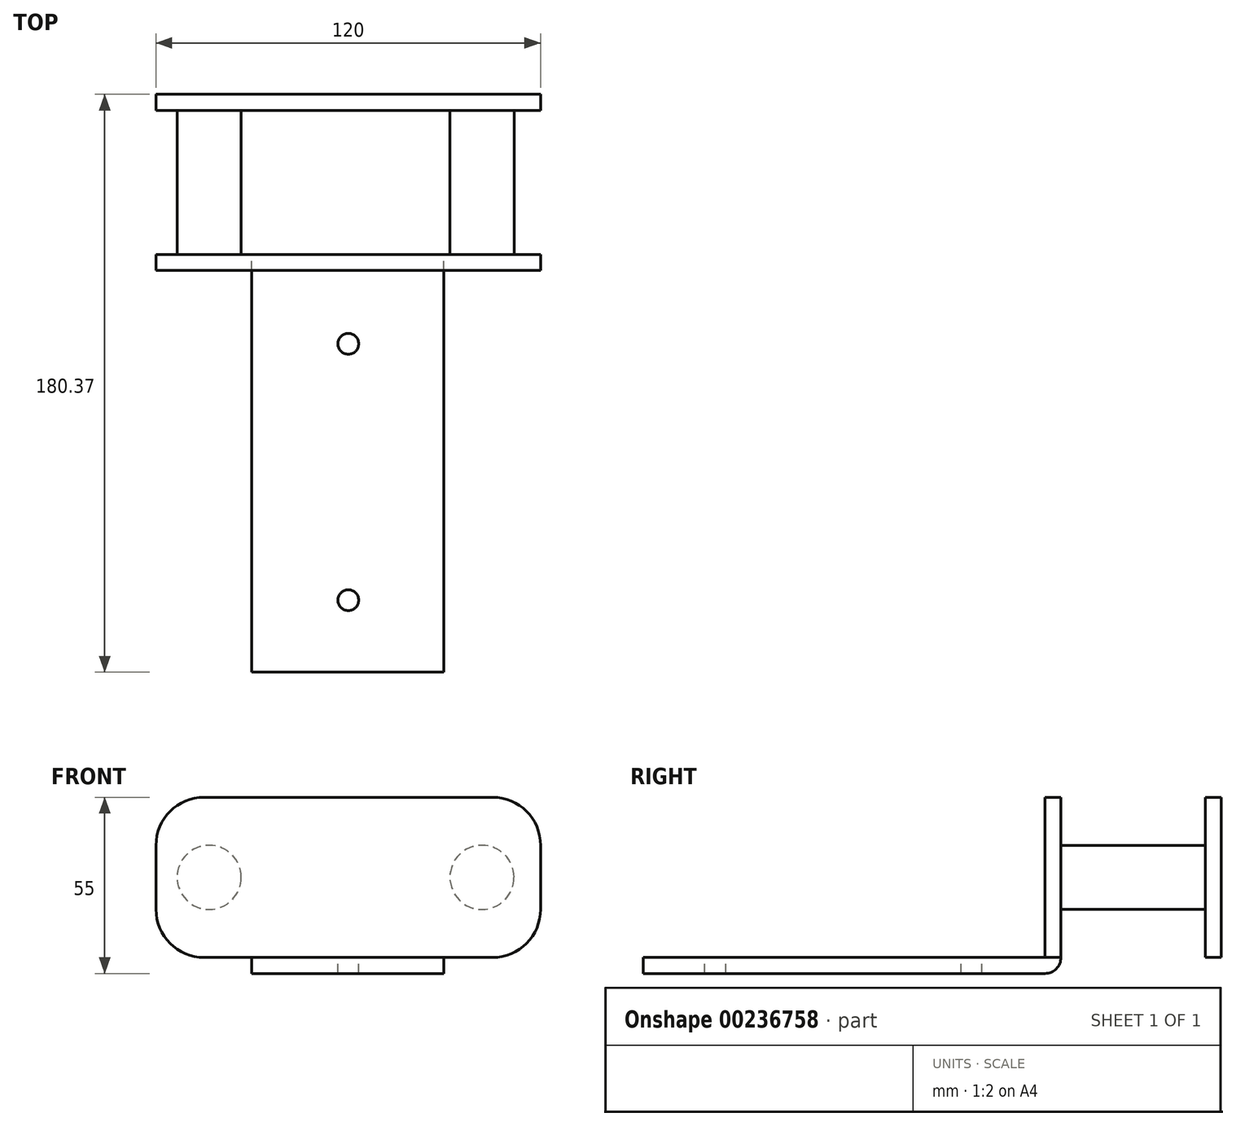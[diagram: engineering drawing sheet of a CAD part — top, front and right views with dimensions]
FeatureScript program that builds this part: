
annotation { "Feature Type Name" : "Feature", "Feature Type Description" : "" }
export const myFeature = defineFeature(function(context is Context, id is Id, definition is map)
    precondition{}
    {
        {
            var Q0;
            Q0=qCreatedBy(makeId("Top.planeOp"),FACE);
            var sketch = newSketch(context, id + "F0", { "sketchPlane" : qUnion([Q0])});
            skLineSegment(sketch, "E0.bottom", {"start": v(29.8, -114.86) * mm, "end": v(-30.2, -114.86) * mm});
            skLineSegment(sketch, "E0.top", {"start": v(29.8, 15.5) * mm, "end": v(-30.2, 15.5) * mm});
            skLineSegment(sketch, "E0.left", {"start": v(29.8, -114.86) * mm, "end": v(29.8, 15.5) * mm});
            skLineSegment(sketch, "E0.right", {"start": v(-30.2, -114.86) * mm, "end": v(-30.2, 15.5) * mm});
            skSolve(sketch);
        }
        {
            var Q0;
            Q0 = qSketchRegion(id + "F0", true);
            extrude(context, id + "F1", {"entities" : qUnion([Q0]), "oppositeDirection" : true, "depth" : 5 * mm, "offsetDistance" : 25 * mm});
        }
        {
            var Q0;
            Q0=makeQuery(id+"F1.opExtrude","SWEPT_FACE",FACE,{"disambiguationData":[OSD([sQuery(id+"F0.wireOp",EDGE,"E0.top")])]});
            var sketch = newSketch(context, id + "F2", { "sketchPlane" : qUnion([Q0])});
            skLineSegment(sketch, "E1.bottom", {"start": v(-45, 0) * mm, "end": v(45, 0) * mm});
            skLineSegment(sketch, "E1.top", {"start": v(-45, 50) * mm, "end": v(45, 50) * mm});
            skLineSegment(sketch, "E1.left", {"start": v(-60, 15) * mm, "end": v(-60, 35) * mm});
            skLineSegment(sketch, "E1.right", {"start": v(60, 15) * mm, "end": v(60, 35) * mm});
            skPoint(sketch, "E2.visualSharp", {"position": v(-60, 50) * mm});
            skArc(sketch, "E2.filletArc", {"start": v(-45, 50) * mm, "mid": v(-55.6, 45.6) * mm, "end": v(-60, 35) * mm});
            skPoint(sketch, "E3.visualSharp", {"position": v(-60, 0) * mm});
            skArc(sketch, "E3.filletArc", {"start": v(-60, 15) * mm, "mid": v(-55.6, 4.4) * mm, "end": v(-45, 0) * mm});
            skPoint(sketch, "E4.visualSharp", {"position": v(60, 0) * mm});
            skArc(sketch, "E4.filletArc", {"start": v(45, 0) * mm, "mid": v(55.6, 4.4) * mm, "end": v(60, 15) * mm});
            skPoint(sketch, "E5.visualSharp", {"position": v(60, 50) * mm});
            skArc(sketch, "E5.filletArc", {"start": v(60, 35) * mm, "mid": v(55.6, 45.6) * mm, "end": v(45, 50) * mm});
            skSolve(sketch);
        }
        {
            var Q0;
            Q0=makeQuery(id+"F2.imprint","IMPRINT",FACE,{"disambiguationData":[TD([[makeQuery(id+"F2.imprint","IMPRINT",EDGE,{"derivedFrom":sQuery(id+"F2.wireOp",EDGE,"E1.top")}),-1.0]])]});
            extrude(context, id + "F3", {"entities" : qUnion([Q0]), "oppositeDirection" : true, "depth" : 5 * mm, "offsetDistance" : 25 * mm});
        }
        {
            var Q0;
            Q0=makeQuery(id+"F3.opExtrude","CAP_FACE",FACE,{"disambiguationData":[OSD([sQuery(id+"F0.wireOp",EDGE,"E0.top"),sQuery(id+"F0.wireOp",EDGE,"E0.left"),sQuery(id+"F0.wireOp",EDGE,"E0.right"),sQuery(id+"F2.wireOp",EDGE,"E1.bottom"),sQuery(id+"F2.wireOp",EDGE,"E1.top"),sQuery(id+"F2.wireOp",EDGE,"E1.left"),sQuery(id+"F2.wireOp",EDGE,"E1.right"),sQuery(id+"F2.wireOp",EDGE,"E2.filletArc"),sQuery(id+"F2.wireOp",EDGE,"E3.filletArc"),sQuery(id+"F2.wireOp",EDGE,"E4.filletArc"),sQuery(id+"F2.wireOp",EDGE,"E5.filletArc")])],"isStart":true});
            var sketch = newSketch(context, id + "F4", { "sketchPlane" : qUnion([Q0])});
            skCircle(sketch, "E6", {"center": v(43.4, 25) * mm, "radius": 10 * mm});
            skPoint(sketch, "E6.centerSnap0", {"position": v(60, 25) * mm});
            skCircle(sketch, "E7", {"center": v(-41.7, 25) * mm, "radius": 10 * mm});
            skSolve(sketch);
        }
        {
            var Q0;
            Q0=makeQuery(id+"F4.imprint","IMPRINT",FACE,{"disambiguationData":[TD([[makeQuery(id+"F4.imprint","IMPRINT",EDGE,{"derivedFrom":sQuery(id+"F4.wireOp",EDGE,"E7")}),1.0]])]});
            var Q1;
            Q1=makeQuery(id+"F4.imprint","IMPRINT",FACE,{"disambiguationData":[TD([[makeQuery(id+"F4.imprint","IMPRINT",EDGE,{"derivedFrom":sQuery(id+"F4.wireOp",EDGE,"E6")}),1.0]])]});
            extrude(context, id + "F5", {"entities" : qUnion([Q0, Q1]), "operationType" : NewBodyOperationType.ADD, "depth" : 50 * mm, "offsetDistance" : 25 * mm});
        }
        {
            var Q0;
            Q0=makeQuery(id+"F5.opExtrude","CAP_FACE",FACE,{"disambiguationData":[OSD([sQuery(id+"F4.wireOp",EDGE,"E7")])],"isStart":false});
            var sketch = newSketch(context, id + "F6", { "sketchPlane" : qUnion([Q0])});
            skLineSegment(sketch, "E8.bottom", {"start": v(45, 0) * mm, "end": v(-45, 0) * mm});
            skLineSegment(sketch, "E8.top", {"start": v(45, 50) * mm, "end": v(-45, 50) * mm});
            skLineSegment(sketch, "E8.left", {"start": v(60, 15) * mm, "end": v(60, 35) * mm});
            skLineSegment(sketch, "E8.right", {"start": v(-60, 15) * mm, "end": v(-60, 35) * mm});
            skPoint(sketch, "E9.visualSharp", {"position": v(-60, 50) * mm});
            skArc(sketch, "E9.filletArc", {"start": v(-45, 50) * mm, "mid": v(-55.6, 45.6) * mm, "end": v(-60, 35) * mm});
            skPoint(sketch, "E10.visualSharp", {"position": v(60, 50) * mm});
            skArc(sketch, "E10.filletArc", {"start": v(60, 35) * mm, "mid": v(55.6, 45.6) * mm, "end": v(45, 50) * mm});
            skPoint(sketch, "E11.visualSharp", {"position": v(60, 0) * mm});
            skArc(sketch, "E11.filletArc", {"start": v(45, 0) * mm, "mid": v(55.6, 4.4) * mm, "end": v(60, 15) * mm});
            skPoint(sketch, "E12.visualSharp", {"position": v(-60, 0) * mm});
            skArc(sketch, "E12.filletArc", {"start": v(-60, 15) * mm, "mid": v(-55.6, 4.4) * mm, "end": v(-45, 0) * mm});
            skSolve(sketch);
        }
        {
            var Q0;
            Q0=makeQuery(id+"F6.imprint","IMPRINT",FACE,{"disambiguationData":[TD([[makeQuery(id+"F6.imprint","IMPRINT",EDGE,{"derivedFrom":sQuery(id+"F6.wireOp",EDGE,"E8.bottom")}),-1.0]])]});
            extrude(context, id + "F7", {"entities" : qUnion([Q0]), "operationType" : NewBodyOperationType.ADD, "oppositeDirection" : true, "depth" : 5 * mm, "offsetDistance" : 25 * mm});
        }
        {
            var Q0;
            Q0=makeQuery(id+"F1.opExtrude","CAP_FACE",FACE,{"disambiguationData":[OSD([sQuery(id+"F0.wireOp",EDGE,"E0.bottom"),sQuery(id+"F0.wireOp",EDGE,"E0.top"),sQuery(id+"F0.wireOp",EDGE,"E0.left"),sQuery(id+"F0.wireOp",EDGE,"E0.right")])],"isStart":false});
            var sketch = newSketch(context, id + "F8", { "sketchPlane" : qUnion([Q0])});
            skPoint(sketch, "E13", {"position": v(0, 92.36) * mm});
            skPoint(sketch, "E14", {"position": v(0, 12.36) * mm});
            skSolve(sketch);
        }
        {
            var Q0;
            Q0=sQuery(id+"F8.wireOp",VERTEX,"E14");
            var Q1;
            Q1=sQuery(id+"F8.wireOp",VERTEX,"E13");
            var Q2;
            Q2=makeQuery(id+"F1.opExtrude","SWEPT_BODY",BODY,{"disambiguationData":[OSD([sQuery(id+"F0.wireOp",EDGE,"E0.bottom"),sQuery(id+"F0.wireOp",EDGE,"E0.top"),sQuery(id+"F0.wireOp",EDGE,"E0.left"),sQuery(id+"F0.wireOp",EDGE,"E0.right")])]});
            hole(context, id + "F9", {"style" : HoleStyle.SIMPLE, "endStyle" : HoleEndStyle.BLIND, "holeDiameter" : 6.5 * mm, "majorDiameter" : 5 * mm, "holeDepth" : 6 * mm, "isTappedThrough" : true, "tappedDepth" : 31.25 * mm, "tapClearance" : 3, "startFromSketch" : true, "locations" : qUnion([Q0, Q1]), "scope" : qUnion([Q2])});
        }
        {
            var Q0;
            Q0=makeQuery(id+"F1.opExtrude","CAP_EDGE",EDGE,{"disambiguationData":[OSD([sQuery(id+"F0.wireOp",EDGE,"E0.top")])],"isStart":false});
            fillet(context, id + "F10", {"entities" : qUnion([Q0]), "tangentPropagation" : true, "radius" : 5 * mm, "defaultsChanged" : false, "vertexSettings" : [], "allowEdgeOverflow" : false});
        }
    });
